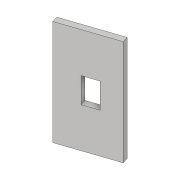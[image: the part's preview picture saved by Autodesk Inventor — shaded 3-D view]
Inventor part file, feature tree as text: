
AUTODESK INVENTOR PART (.ipt)
format: ipt  version: 2018.3 (Build 223284000, 284)  size: 90,624 bytes
history: native  units: in
note: dims shown in document units (in); Inventor stores cm internally (conversion verified against a paired STEP export)
features: extrude x2, sketch x2
ambient origin geometry x8: Origin, YZ Plane, XZ Plane, XY Plane, X Axis, Y Axis, Z Axis, Center Point
bodies: Solid1 (feature_tree)
feature tree (4):
  extrude  "Extrusion1"  Depth=0.118in
  extrude  "Extrusion2"  Depth=0.3in
  sketch  "Sketch1"  dims[d0=1.1in d3=2.079in d4=0.0in d5=0.118in]
  sketch  "Sketch2"  dims[d9=0.5in d10=0.3in d13=0.7895in d14=0.7895in d16=1.0in d17=0.0in d18=0.7393in]
